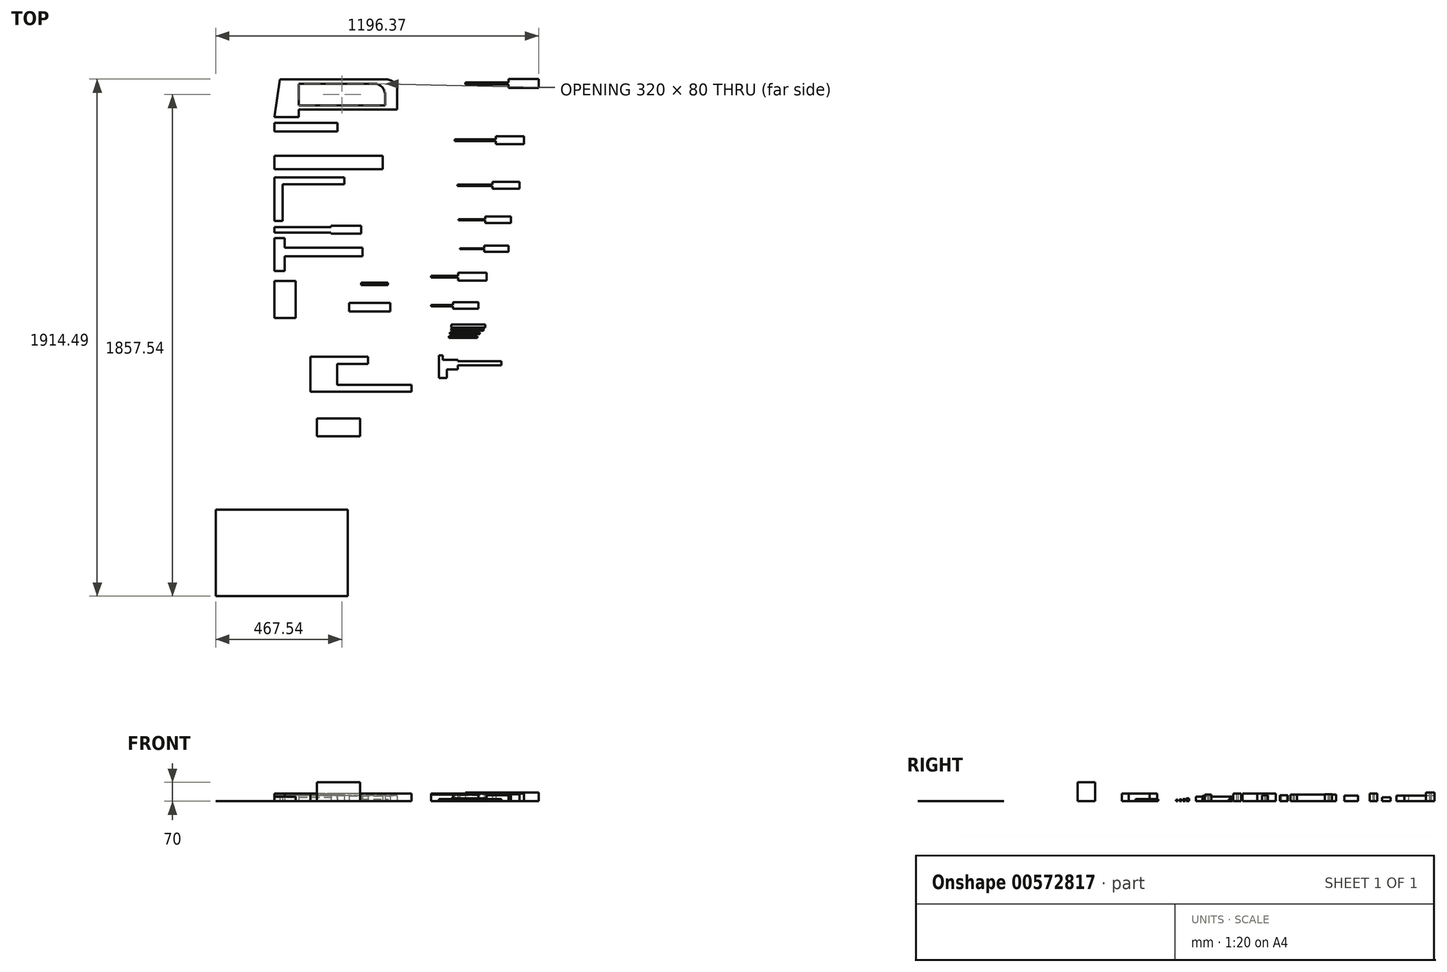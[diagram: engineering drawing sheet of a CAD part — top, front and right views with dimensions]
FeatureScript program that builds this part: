
annotation { "Feature Type Name" : "Feature", "Feature Type Description" : "" }
export const myFeature = defineFeature(function(context is Context, id is Id, definition is map)
    precondition{}
    {
        {
            var Q0;
            Q0=qCreatedBy(makeId("Top.planeOp"),FACE);
            var sketch = newSketch(context, id + "F0", { "sketchPlane" : qUnion([Q0])});
            skLineSegment(sketch, "E0", {"start": v(455, 29) * mm, "end": v(455, 100) * mm});
            skLineSegment(sketch, "E1", {"start": v(415, 140) * mm, "end": v(20, 140) * mm});
            skLineSegment(sketch, "E2", {"start": v(20, 140) * mm, "end": v(0, 0) * mm});
            skLineSegment(sketch, "E3", {"start": v(90, 124) * mm, "end": v(90, 44) * mm});
            skLineSegment(sketch, "E4", {"start": v(90, 44) * mm, "end": v(410, 44) * mm});
            skLineSegment(sketch, "E5", {"start": v(410, 44) * mm, "end": v(410, 84) * mm});
            skLineSegment(sketch, "E6", {"start": v(370, 124) * mm, "end": v(90, 124) * mm});
            skLineSegment(sketch, "E7", {"start": v(0, 0) * mm, "end": v(90, 0) * mm});
            skLineSegment(sketch, "E8", {"start": v(90, 0) * mm, "end": v(90, 29) * mm});
            skLineSegment(sketch, "E9", {"start": v(90, 29) * mm, "end": v(455, 29) * mm});
            skPoint(sketch, "E10.visualSharp", {"position": v(410, 124) * mm});
            skArc(sketch, "E10.filletArc", {"start": v(410, 84) * mm, "mid": v(398.28, 112.28) * mm, "end": v(370, 124) * mm});
            skPoint(sketch, "E11.visualSharp", {"position": v(455, 140) * mm});
            skArc(sketch, "E11.filletArc", {"start": v(455, 100) * mm, "mid": v(443.28, 128.28) * mm, "end": v(415, 140) * mm});
            skSolve(sketch);
        }
        {
            var Q0;
            Q0 = qSketchRegion(id + "F0", true);
            extrude(context, id + "F1", {"entities" : qUnion([Q0]), "depth" : 21 * mm, "offsetDistance" : 25 * mm});
        }
        {
            var Q0;
            Q0=qCreatedBy(makeId("Top.planeOp"),FACE);
            var sketch = newSketch(context, id + "F2", { "sketchPlane" : qUnion([Q0])});
            skLineSegment(sketch, "E12.bottom", {"start": v(0, -21.6) * mm, "end": v(234, -21.6) * mm});
            skLineSegment(sketch, "E12.top", {"start": v(0, -53.1) * mm, "end": v(234, -53.1) * mm});
            skLineSegment(sketch, "E12.left", {"start": v(0, -21.6) * mm, "end": v(0, -53.1) * mm});
            skLineSegment(sketch, "E12.right", {"start": v(234, -21.6) * mm, "end": v(234, -53.1) * mm});
            skSolve(sketch);
        }
        {
            var Q0;
            Q0 = qSketchRegion(id + "F2", true);
            extrude(context, id + "F3", {"entities" : qUnion([Q0]), "depth" : 15 * mm, "offsetDistance" : 25 * mm});
        }
        {
            var Q0;
            Q0=qCreatedBy(makeId("Top.planeOp"),FACE);
            var sketch = newSketch(context, id + "F4", { "sketchPlane" : qUnion([Q0])});
            skLineSegment(sketch, "E13.bottom", {"start": v(0, -142.35) * mm, "end": v(402, -142.35) * mm});
            skLineSegment(sketch, "E13.top", {"start": v(0, -192.85) * mm, "end": v(402, -192.85) * mm});
            skLineSegment(sketch, "E13.left", {"start": v(0, -142.35) * mm, "end": v(0, -192.85) * mm});
            skLineSegment(sketch, "E13.right", {"start": v(402, -142.35) * mm, "end": v(402, -192.85) * mm});
            skSolve(sketch);
        }
        {
            var Q0;
            Q0 = qSketchRegion(id + "F4", true);
            extrude(context, id + "F5", {"entities" : qUnion([Q0]), "depth" : 20.5 * mm, "offsetDistance" : 25 * mm});
        }
        {
            var Q0;
            Q0=qCreatedBy(makeId("Top.planeOp"),FACE);
            var sketch = newSketch(context, id + "F6", { "sketchPlane" : qUnion([Q0])});
            skLineSegment(sketch, "E14", {"start": v(259, -223) * mm, "end": v(0, -223) * mm});
            skLineSegment(sketch, "E15", {"start": v(0, -223) * mm, "end": v(0, -384) * mm});
            skLineSegment(sketch, "E16", {"start": v(0, -384) * mm, "end": v(30.5, -384) * mm});
            skLineSegment(sketch, "E17", {"start": v(30.5, -384) * mm, "end": v(30.5, -248) * mm});
            skLineSegment(sketch, "E18", {"start": v(30.5, -248) * mm, "end": v(259, -248) * mm});
            skLineSegment(sketch, "E19", {"start": v(259, -248) * mm, "end": v(259, -223) * mm});
            skSolve(sketch);
        }
        {
            var Q0;
            Q0 = qSketchRegion(id + "F6", true);
            extrude(context, id + "F7", {"entities" : qUnion([Q0]), "depth" : 25 * mm, "offsetDistance" : 25 * mm});
        }
        {
            var Q0;
            Q0=qCreatedBy(makeId("Top.planeOp"),FACE);
            var sketch = newSketch(context, id + "F8", { "sketchPlane" : qUnion([Q0])});
            skLineSegment(sketch, "E20", {"start": v(0, -407.04) * mm, "end": v(0, -427.04) * mm});
            skLineSegment(sketch, "E21", {"start": v(0, -427.04) * mm, "end": v(210, -427.04) * mm});
            skLineSegment(sketch, "E22", {"start": v(210, -427.04) * mm, "end": v(210, -431.54) * mm});
            skLineSegment(sketch, "E23", {"start": v(210, -431.54) * mm, "end": v(321, -431.54) * mm});
            skLineSegment(sketch, "E24", {"start": v(321, -431.54) * mm, "end": v(321, -402.54) * mm});
            skLineSegment(sketch, "E25", {"start": v(321, -402.54) * mm, "end": v(210, -402.54) * mm});
            skLineSegment(sketch, "E26", {"start": v(210, -402.54) * mm, "end": v(210, -407.04) * mm});
            skLineSegment(sketch, "E27", {"start": v(210, -407.04) * mm, "end": v(0, -407.04) * mm});
            skSolve(sketch);
        }
        {
            var Q0;
            Q0 = qSketchRegion(id + "F8", true);
            extrude(context, id + "F9", {"entities" : qUnion([Q0]), "depth" : 21.5 * mm, "offsetDistance" : 25 * mm});
        }
        {
            var Q0;
            Q0=qCreatedBy(makeId("Top.planeOp"),FACE);
            var sketch = newSketch(context, id + "F10", { "sketchPlane" : qUnion([Q0])});
            skLineSegment(sketch, "E28", {"start": v(0, -447.14) * mm, "end": v(0, -569.64) * mm});
            skLineSegment(sketch, "E29", {"start": v(0, -569.64) * mm, "end": v(38.5, -569.64) * mm});
            skLineSegment(sketch, "E30", {"start": v(38.5, -569.64) * mm, "end": v(38.5, -515.64) * mm});
            skLineSegment(sketch, "E31", {"start": v(38.5, -515.64) * mm, "end": v(326.5, -515.64) * mm});
            skLineSegment(sketch, "E32", {"start": v(326.5, -515.64) * mm, "end": v(326.5, -483.14) * mm});
            skLineSegment(sketch, "E33", {"start": v(326.5, -483.14) * mm, "end": v(38.5, -483.14) * mm});
            skLineSegment(sketch, "E34", {"start": v(38.5, -483.14) * mm, "end": v(38.5, -447.14) * mm});
            skLineSegment(sketch, "E35", {"start": v(38.5, -447.14) * mm, "end": v(0, -447.14) * mm});
            skSolve(sketch);
        }
        {
            var Q0;
            Q0 = qSketchRegion(id + "F10", true);
            extrude(context, id + "F11", {"entities" : qUnion([Q0]), "depth" : 28 * mm, "offsetDistance" : 25 * mm});
        }
        {
            var Q0;
            Q0=qCreatedBy(makeId("Top.planeOp"),FACE);
            var sketch = newSketch(context, id + "F12", { "sketchPlane" : qUnion([Q0])});
            skLineSegment(sketch, "E36.bottom", {"start": v(0, -606.7) * mm, "end": v(79, -606.7) * mm});
            skLineSegment(sketch, "E36.top", {"start": v(0, -743.2) * mm, "end": v(79, -743.2) * mm});
            skLineSegment(sketch, "E36.left", {"start": v(0, -606.7) * mm, "end": v(0, -743.2) * mm});
            skLineSegment(sketch, "E36.right", {"start": v(79, -606.7) * mm, "end": v(79, -743.2) * mm});
            skSolve(sketch);
        }
        {
            var Q0;
            Q0 = qSketchRegion(id + "F12", true);
            extrude(context, id + "F13", {"entities" : qUnion([Q0]), "depth" : 16.5 * mm, "offsetDistance" : 25 * mm});
        }
        {
            var Q0;
            Q0=qCreatedBy(makeId("Top.planeOp"),FACE);
            var sketch = newSketch(context, id + "F14", { "sketchPlane" : qUnion([Q0])});
            skLineSegment(sketch, "E37", {"start": v(707.83, 128.45) * mm, "end": v(707.83, 121.45) * mm});
            skLineSegment(sketch, "E38", {"start": v(707.83, 121.45) * mm, "end": v(867.83, 121.45) * mm});
            skLineSegment(sketch, "E39", {"start": v(867.83, 121.45) * mm, "end": v(867.83, 108.95) * mm});
            skLineSegment(sketch, "E40", {"start": v(867.83, 108.95) * mm, "end": v(978.83, 108.95) * mm});
            skLineSegment(sketch, "E41", {"start": v(978.83, 108.95) * mm, "end": v(978.83, 140.95) * mm});
            skLineSegment(sketch, "E42", {"start": v(978.83, 140.95) * mm, "end": v(867.83, 140.95) * mm});
            skLineSegment(sketch, "E43", {"start": v(867.83, 140.95) * mm, "end": v(867.83, 128.45) * mm});
            skLineSegment(sketch, "E44", {"start": v(867.83, 128.45) * mm, "end": v(707.83, 128.45) * mm});
            skSolve(sketch);
        }
        {
            var Q0;
            Q0 = qSketchRegion(id + "F14", true);
            extrude(context, id + "F15", {"entities" : qUnion([Q0]), "depth" : 32 * mm, "offsetDistance" : 25 * mm});
        }
        {
            var Q0;
            Q0=qCreatedBy(makeId("Top.planeOp"),FACE);
            var sketch = newSketch(context, id + "F16", { "sketchPlane" : qUnion([Q0])});
            skLineSegment(sketch, "E45", {"start": v(667.7, -82.08) * mm, "end": v(820.26, -82.08) * mm});
            skLineSegment(sketch, "E46", {"start": v(820.26, -82.08) * mm, "end": v(820.26, -70.58) * mm});
            skLineSegment(sketch, "E47", {"start": v(820.26, -70.58) * mm, "end": v(925.26, -70.58) * mm});
            skLineSegment(sketch, "E48", {"start": v(925.26, -70.58) * mm, "end": v(925.26, -99.58) * mm});
            skLineSegment(sketch, "E49", {"start": v(925.26, -99.58) * mm, "end": v(820.26, -99.58) * mm});
            skLineSegment(sketch, "E50", {"start": v(820.26, -99.58) * mm, "end": v(820.26, -88.08) * mm});
            skLineSegment(sketch, "E51", {"start": v(820.26, -88.08) * mm, "end": v(667.7, -88.08) * mm});
            skLineSegment(sketch, "E52", {"start": v(667.7, -88.08) * mm, "end": v(667.7, -82.08) * mm});
            skSolve(sketch);
        }
        {
            var Q0;
            Q0 = qSketchRegion(id + "F16", true);
            extrude(context, id + "F17", {"entities" : qUnion([Q0]), "depth" : 29 * mm, "offsetDistance" : 25 * mm});
        }
        {
            var Q0;
            Q0=qCreatedBy(makeId("Top.planeOp"),FACE);
            var sketch = newSketch(context, id + "F18", { "sketchPlane" : qUnion([Q0])});
            skLineSegment(sketch, "E53", {"start": v(678.14, -249.36) * mm, "end": v(808.14, -249.36) * mm});
            skLineSegment(sketch, "E54", {"start": v(808.14, -249.36) * mm, "end": v(808.14, -238.86) * mm});
            skLineSegment(sketch, "E55", {"start": v(808.14, -238.86) * mm, "end": v(908.14, -238.86) * mm});
            skLineSegment(sketch, "E56", {"start": v(908.14, -238.86) * mm, "end": v(908.14, -264.86) * mm});
            skLineSegment(sketch, "E57", {"start": v(908.14, -264.86) * mm, "end": v(808.14, -264.86) * mm});
            skLineSegment(sketch, "E58", {"start": v(808.14, -264.86) * mm, "end": v(808.14, -254.36) * mm});
            skLineSegment(sketch, "E59", {"start": v(808.14, -254.36) * mm, "end": v(678.14, -254.36) * mm});
            skLineSegment(sketch, "E60", {"start": v(678.14, -254.36) * mm, "end": v(678.14, -249.36) * mm});
            skSolve(sketch);
        }
        {
            var Q0;
            Q0 = qSketchRegion(id + "F18", true);
            extrude(context, id + "F19", {"entities" : qUnion([Q0]), "depth" : 26 * mm, "offsetDistance" : 25 * mm});
        }
        {
            var Q0;
            Q0=qCreatedBy(makeId("Top.planeOp"),FACE);
            var sketch = newSketch(context, id + "F20", { "sketchPlane" : qUnion([Q0])});
            skLineSegment(sketch, "E61", {"start": v(681.79, -378.3) * mm, "end": v(781.79, -378.3) * mm});
            skLineSegment(sketch, "E62", {"start": v(781.79, -378.3) * mm, "end": v(781.79, -368.3) * mm});
            skLineSegment(sketch, "E63", {"start": v(781.79, -368.3) * mm, "end": v(875.79, -368.3) * mm});
            skLineSegment(sketch, "E64", {"start": v(875.79, -368.3) * mm, "end": v(875.79, -392.3) * mm});
            skLineSegment(sketch, "E65", {"start": v(875.79, -392.3) * mm, "end": v(781.79, -392.3) * mm});
            skLineSegment(sketch, "E66", {"start": v(781.79, -392.3) * mm, "end": v(781.79, -382.3) * mm});
            skLineSegment(sketch, "E67", {"start": v(781.79, -382.3) * mm, "end": v(681.79, -382.3) * mm});
            skLineSegment(sketch, "E68", {"start": v(681.79, -382.3) * mm, "end": v(681.79, -378.3) * mm});
            skSolve(sketch);
        }
        {
            var Q0;
            Q0 = qSketchRegion(id + "F20", true);
            extrude(context, id + "F21", {"entities" : qUnion([Q0]), "depth" : 24 * mm, "offsetDistance" : 25 * mm});
        }
        {
            var Q0;
            Q0=qCreatedBy(makeId("Top.planeOp"),FACE);
            var sketch = newSketch(context, id + "F22", { "sketchPlane" : qUnion([Q0])});
            skLineSegment(sketch, "E69", {"start": v(687.02, -485.23) * mm, "end": v(777.02, -485.23) * mm});
            skLineSegment(sketch, "E70", {"start": v(777.02, -485.23) * mm, "end": v(777.02, -475.98) * mm});
            skLineSegment(sketch, "E71", {"start": v(777.02, -475.98) * mm, "end": v(867.02, -475.98) * mm});
            skLineSegment(sketch, "E72", {"start": v(867.02, -475.98) * mm, "end": v(867.02, -497.98) * mm});
            skLineSegment(sketch, "E73", {"start": v(867.02, -497.98) * mm, "end": v(777.02, -497.98) * mm});
            skLineSegment(sketch, "E74", {"start": v(777.02, -497.98) * mm, "end": v(777.02, -488.73) * mm});
            skLineSegment(sketch, "E75", {"start": v(777.02, -488.73) * mm, "end": v(687.02, -488.73) * mm});
            skLineSegment(sketch, "E76", {"start": v(687.02, -488.73) * mm, "end": v(687.02, -485.23) * mm});
            skSolve(sketch);
        }
        {
            var Q0;
            Q0 = qSketchRegion(id + "F22", true);
            extrude(context, id + "F23", {"entities" : qUnion([Q0]), "depth" : 22 * mm, "offsetDistance" : 25 * mm});
        }
        {
            var Q0;
            Q0=qCreatedBy(makeId("Top.planeOp"),FACE);
            var sketch = newSketch(context, id + "F24", { "sketchPlane" : qUnion([Q0])});
            skLineSegment(sketch, "E77", {"start": v(580.39, -587.35) * mm, "end": v(681.39, -587.35) * mm});
            skLineSegment(sketch, "E78", {"start": v(681.39, -587.35) * mm, "end": v(681.39, -575.85) * mm});
            skLineSegment(sketch, "E79", {"start": v(681.39, -575.85) * mm, "end": v(786.39, -575.85) * mm});
            skLineSegment(sketch, "E80", {"start": v(786.39, -575.85) * mm, "end": v(786.39, -604.85) * mm});
            skLineSegment(sketch, "E81", {"start": v(786.39, -604.85) * mm, "end": v(681.39, -604.85) * mm});
            skLineSegment(sketch, "E82", {"start": v(681.39, -604.85) * mm, "end": v(681.39, -593.35) * mm});
            skLineSegment(sketch, "E83", {"start": v(681.39, -593.35) * mm, "end": v(580.39, -593.35) * mm});
            skLineSegment(sketch, "E84", {"start": v(580.39, -593.35) * mm, "end": v(580.39, -587.35) * mm});
            skSolve(sketch);
        }
        {
            var Q0;
            Q0 = qSketchRegion(id + "F24", true);
            extrude(context, id + "F25", {"entities" : qUnion([Q0]), "depth" : 29 * mm, "offsetDistance" : 25 * mm});
        }
        {
            var Q0;
            Q0=qCreatedBy(makeId("Top.planeOp"),FACE);
            var sketch = newSketch(context, id + "F26", { "sketchPlane" : qUnion([Q0])});
            skLineSegment(sketch, "E85", {"start": v(580.22, -695.15) * mm, "end": v(661.22, -695.15) * mm});
            skLineSegment(sketch, "E86", {"start": v(661.22, -695.15) * mm, "end": v(661.22, -685.65) * mm});
            skLineSegment(sketch, "E87", {"start": v(661.22, -685.65) * mm, "end": v(756.22, -685.65) * mm});
            skLineSegment(sketch, "E88", {"start": v(756.22, -685.65) * mm, "end": v(756.22, -709.65) * mm});
            skLineSegment(sketch, "E89", {"start": v(756.22, -709.65) * mm, "end": v(661.22, -709.65) * mm});
            skLineSegment(sketch, "E90", {"start": v(661.22, -709.65) * mm, "end": v(661.22, -700.15) * mm});
            skLineSegment(sketch, "E91", {"start": v(661.22, -700.15) * mm, "end": v(580.22, -700.15) * mm});
            skLineSegment(sketch, "E92", {"start": v(580.22, -700.15) * mm, "end": v(580.22, -695.15) * mm});
            skSolve(sketch);
        }
        {
            var Q0;
            Q0 = qSketchRegion(id + "F26", true);
            extrude(context, id + "F27", {"entities" : qUnion([Q0]), "depth" : 24 * mm, "offsetDistance" : 25 * mm});
        }
        {
            var Q0;
            Q0=qCreatedBy(makeId("Top.planeOp"),FACE);
            var sketch = newSketch(context, id + "F28", { "sketchPlane" : qUnion([Q0])});
            skLineSegment(sketch, "E93.bottom", {"start": v(655.89, -768.28) * mm, "end": v(780.89, -768.28) * mm});
            skLineSegment(sketch, "E93.top", {"start": v(655.89, -778.78) * mm, "end": v(780.89, -778.78) * mm});
            skLineSegment(sketch, "E93.left", {"start": v(655.89, -768.28) * mm, "end": v(655.89, -778.78) * mm});
            skLineSegment(sketch, "E93.right", {"start": v(780.89, -768.28) * mm, "end": v(780.89, -778.78) * mm});
            skSolve(sketch);
        }
        {
            var Q0;
            Q0 = qSketchRegion(id + "F28", true);
            extrude(context, id + "F29", {"entities" : qUnion([Q0]), "depth" : 10.5 * mm, "offsetDistance" : 25 * mm});
        }
        {
            var Q0;
            Q0=qCreatedBy(makeId("Top.planeOp"),FACE);
            var sketch = newSketch(context, id + "F30", { "sketchPlane" : qUnion([Q0])});
            skLineSegment(sketch, "E94.bottom", {"start": v(655.35, -782.35) * mm, "end": v(775.35, -782.35) * mm});
            skLineSegment(sketch, "E94.top", {"start": v(655.35, -790.85) * mm, "end": v(775.35, -790.85) * mm});
            skLineSegment(sketch, "E94.left", {"start": v(655.35, -782.35) * mm, "end": v(655.35, -790.85) * mm});
            skLineSegment(sketch, "E94.right", {"start": v(775.35, -782.35) * mm, "end": v(775.35, -790.85) * mm});
            skSolve(sketch);
        }
        {
            var Q0;
            Q0 = qSketchRegion(id + "F30", true);
            extrude(context, id + "F31", {"entities" : qUnion([Q0]), "depth" : 8.5 * mm, "offsetDistance" : 25 * mm});
        }
        {
            var Q0;
            Q0=qCreatedBy(makeId("Top.planeOp"),FACE);
            var sketch = newSketch(context, id + "F32", { "sketchPlane" : qUnion([Q0])});
            skLineSegment(sketch, "E95.bottom", {"start": v(650.74, -796.72) * mm, "end": v(760.74, -796.72) * mm});
            skLineSegment(sketch, "E95.top", {"start": v(650.74, -803.72) * mm, "end": v(760.74, -803.72) * mm});
            skLineSegment(sketch, "E95.left", {"start": v(650.74, -796.72) * mm, "end": v(650.74, -803.72) * mm});
            skLineSegment(sketch, "E95.right", {"start": v(760.74, -796.72) * mm, "end": v(760.74, -803.72) * mm});
            skSolve(sketch);
        }
        {
            var Q0;
            Q0 = qSketchRegion(id + "F32", true);
            extrude(context, id + "F33", {"entities" : qUnion([Q0]), "depth" : 7 * mm, "offsetDistance" : 25 * mm});
        }
        {
            var Q0;
            Q0=qCreatedBy(makeId("Top.planeOp"),FACE);
            var sketch = newSketch(context, id + "F34", { "sketchPlane" : qUnion([Q0])});
            skLineSegment(sketch, "E96.bottom", {"start": v(647.06, -810.7) * mm, "end": v(752.06, -810.7) * mm});
            skLineSegment(sketch, "E96.top", {"start": v(647.06, -816.7) * mm, "end": v(752.06, -816.7) * mm});
            skLineSegment(sketch, "E96.left", {"start": v(647.06, -810.7) * mm, "end": v(647.06, -816.7) * mm});
            skLineSegment(sketch, "E96.right", {"start": v(752.06, -810.7) * mm, "end": v(752.06, -816.7) * mm});
            skSolve(sketch);
        }
        {
            var Q0;
            Q0 = qSketchRegion(id + "F34", true);
            extrude(context, id + "F35", {"entities" : qUnion([Q0]), "depth" : 6 * mm, "offsetDistance" : 25 * mm});
        }
        {
            var Q0;
            Q0=qCreatedBy(makeId("Top.planeOp"),FACE);
            var sketch = newSketch(context, id + "F36", { "sketchPlane" : qUnion([Q0])});
            skLineSegment(sketch, "E97.bottom", {"start": v(320.88, -612.63) * mm, "end": v(420.88, -612.63) * mm});
            skLineSegment(sketch, "E97.top", {"start": v(320.88, -621.13) * mm, "end": v(420.88, -621.13) * mm});
            skLineSegment(sketch, "E97.left", {"start": v(320.88, -612.63) * mm, "end": v(320.88, -621.13) * mm});
            skLineSegment(sketch, "E97.right", {"start": v(420.88, -612.63) * mm, "end": v(420.88, -621.13) * mm});
            skSolve(sketch);
        }
        {
            var Q0;
            Q0 = qSketchRegion(id + "F36", true);
            extrude(context, id + "F37", {"entities" : qUnion([Q0]), "depth" : 8.5 * mm, "offsetDistance" : 25 * mm});
        }
        {
            var Q0;
            Q0=qCreatedBy(makeId("Top.planeOp"),FACE);
            var sketch = newSketch(context, id + "F38", { "sketchPlane" : qUnion([Q0])});
            skLineSegment(sketch, "E98.bottom", {"start": v(276.83, -687.16) * mm, "end": v(429.83, -687.16) * mm});
            skLineSegment(sketch, "E98.top", {"start": v(276.83, -719.16) * mm, "end": v(429.83, -719.16) * mm});
            skLineSegment(sketch, "E98.left", {"start": v(276.83, -687.16) * mm, "end": v(276.83, -719.16) * mm});
            skLineSegment(sketch, "E98.right", {"start": v(429.83, -687.16) * mm, "end": v(429.83, -719.16) * mm});
            skSolve(sketch);
        }
        {
            var Q0;
            Q0 = qSketchRegion(id + "F38", true);
            extrude(context, id + "F39", {"entities" : qUnion([Q0]), "depth" : 19 * mm, "offsetDistance" : 25 * mm});
        }
        {
            var Q0;
            Q0=qCreatedBy(makeId("Top.planeOp"),FACE);
            var sketch = newSketch(context, id + "F40", { "sketchPlane" : qUnion([Q0])});
            skLineSegment(sketch, "E99", {"start": v(508.3, -1016.88) * mm, "end": v(133.3, -1016.88) * mm});
            skLineSegment(sketch, "E100", {"start": v(133.3, -1016.88) * mm, "end": v(133.3, -886.88) * mm});
            skLineSegment(sketch, "E101", {"start": v(133.3, -886.88) * mm, "end": v(347.34, -886.88) * mm});
            skLineSegment(sketch, "E102", {"start": v(347.34, -886.88) * mm, "end": v(347.34, -913.88) * mm});
            skLineSegment(sketch, "E103", {"start": v(347.34, -913.88) * mm, "end": v(232.34, -913.88) * mm});
            skLineSegment(sketch, "E104", {"start": v(232.34, -913.88) * mm, "end": v(232.34, -991.88) * mm});
            skLineSegment(sketch, "E105", {"start": v(232.34, -991.88) * mm, "end": v(508.3, -991.88) * mm});
            skLineSegment(sketch, "E106", {"start": v(508.3, -991.88) * mm, "end": v(508.3, -1016.88) * mm});
            skSolve(sketch);
        }
        {
            var Q0;
            Q0 = qSketchRegion(id + "F40", true);
            extrude(context, id + "F41", {"entities" : qUnion([Q0]), "depth" : 29 * mm, "offsetDistance" : 25 * mm});
        }
        {
            var Q0;
            Q0=qCreatedBy(makeId("Top.planeOp"),FACE);
            var sketch = newSketch(context, id + "F42", { "sketchPlane" : qUnion([Q0])});
            skLineSegment(sketch, "E107.bottom", {"start": v(158.08, -1116.17) * mm, "end": v(318.08, -1116.17) * mm});
            skLineSegment(sketch, "E107.top", {"start": v(158.08, -1181.17) * mm, "end": v(318.08, -1181.17) * mm});
            skLineSegment(sketch, "E107.left", {"start": v(158.08, -1116.17) * mm, "end": v(158.08, -1181.17) * mm});
            skLineSegment(sketch, "E107.right", {"start": v(318.08, -1116.17) * mm, "end": v(318.08, -1181.17) * mm});
            skSolve(sketch);
        }
        {
            var Q0;
            Q0 = qSketchRegion(id + "F42", true);
            extrude(context, id + "F43", {"entities" : qUnion([Q0]), "depth" : 70 * mm, "offsetDistance" : 25 * mm});
        }
        {
            var Q0;
            Q0=qCreatedBy(makeId("Top.planeOp"),FACE);
            var sketch = newSketch(context, id + "F44", { "sketchPlane" : qUnion([Q0])});
            skLineSegment(sketch, "E108", {"start": v(841.29, -903.43) * mm, "end": v(679.29, -903.43) * mm});
            skLineSegment(sketch, "E109", {"start": v(679.29, -903.43) * mm, "end": v(679.29, -898.93) * mm});
            skLineSegment(sketch, "E110", {"start": v(679.29, -898.93) * mm, "end": v(624.29, -898.93) * mm});
            skLineSegment(sketch, "E111", {"start": v(624.29, -898.93) * mm, "end": v(624.29, -882.43) * mm});
            skLineSegment(sketch, "E112", {"start": v(624.29, -882.43) * mm, "end": v(610.29, -882.43) * mm});
            skLineSegment(sketch, "E113", {"start": v(610.29, -882.43) * mm, "end": v(610.29, -966.43) * mm});
            skLineSegment(sketch, "E114", {"start": v(610.29, -966.43) * mm, "end": v(639.29, -966.43) * mm});
            skLineSegment(sketch, "E115", {"start": v(639.29, -966.43) * mm, "end": v(639.29, -934.43) * mm});
            skLineSegment(sketch, "E116", {"start": v(639.29, -934.43) * mm, "end": v(679.29, -934.43) * mm});
            skLineSegment(sketch, "E117", {"start": v(679.29, -934.43) * mm, "end": v(679.29, -919.43) * mm});
            skLineSegment(sketch, "E118", {"start": v(679.29, -919.43) * mm, "end": v(841.29, -919.43) * mm});
            skLineSegment(sketch, "E119", {"start": v(841.29, -919.43) * mm, "end": v(841.29, -903.43) * mm});
            skSolve(sketch);
        }
        {
            var Q0;
            Q0 = qSketchRegion(id + "F44", true);
            extrude(context, id + "F45", {"entities" : qUnion([Q0]), "depth" : 8 * mm, "offsetDistance" : 25 * mm});
        }
        {
            var Q0;
            Q0=qCreatedBy(makeId("Top.planeOp"),FACE);
            var sketch = newSketch(context, id + "F46", { "sketchPlane" : qUnion([Q0])});
            skLineSegment(sketch, "E120.bottom", {"start": v(-217.54, -1453.54) * mm, "end": v(272.46, -1453.54) * mm});
            skLineSegment(sketch, "E120.top", {"start": v(-217.54, -1773.54) * mm, "end": v(272.46, -1773.54) * mm});
            skLineSegment(sketch, "E120.left", {"start": v(-217.54, -1453.54) * mm, "end": v(-217.54, -1773.54) * mm});
            skLineSegment(sketch, "E120.right", {"start": v(272.46, -1453.54) * mm, "end": v(272.46, -1773.54) * mm});
            skSolve(sketch);
        }
        {
            var Q0;
            Q0 = qSketchRegion(id + "F46", true);
            extrude(context, id + "F47", {"entities" : qUnion([Q0]), "depth" : 1 * mm, "offsetDistance" : 25 * mm});
        }
    });
